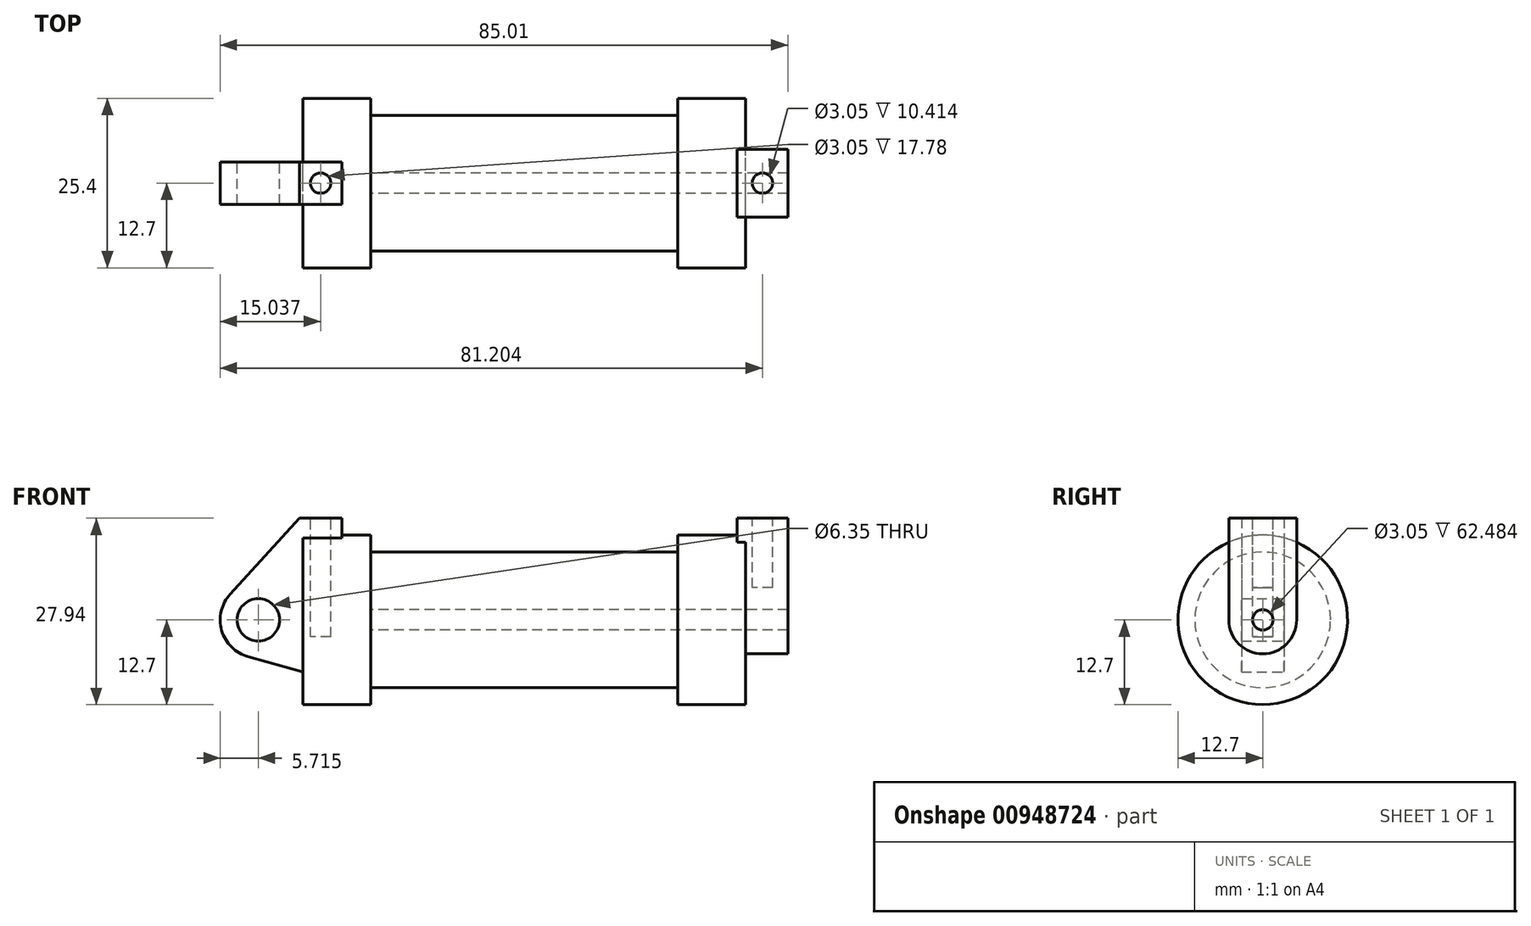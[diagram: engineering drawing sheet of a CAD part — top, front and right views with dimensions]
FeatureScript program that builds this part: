
annotation { "Feature Type Name" : "Feature", "Feature Type Description" : "" }
export const myFeature = defineFeature(function(context is Context, id is Id, definition is map)
    precondition{}
    {
        {
            var Q0;
            Q0=qCreatedBy(makeId("Front.planeOp"),FACE);
            var sketch = newSketch(context, id + "F0", { "sketchPlane" : qUnion([Q0])});
            skLineSegment(sketch, "E0", {"start": v(0, 0) * mm, "end": v(0, 12.7) * mm});
            skLineSegment(sketch, "E1", {"start": v(0, 12.7) * mm, "end": v(10.16, 12.7) * mm});
            skLineSegment(sketch, "E2", {"start": v(10.16, 12.7) * mm, "end": v(10.16, 10.16) * mm});
            skLineSegment(sketch, "E3", {"start": v(10.16, 10.16) * mm, "end": v(56.13, 10.16) * mm});
            skLineSegment(sketch, "E4", {"start": v(56.13, 10.16) * mm, "end": v(56.13, 12.7) * mm});
            skLineSegment(sketch, "E5", {"start": v(56.13, 12.7) * mm, "end": v(66.3, 12.7) * mm});
            skLineSegment(sketch, "E6", {"start": v(66.3, 12.7) * mm, "end": v(66.3, 0) * mm});
            skLineSegment(sketch, "E7", {"start": v(66.3, 0) * mm, "end": v(0, 0) * mm});
            skLineSegment(sketch, "E8", {"start": v(5.84, 15.24) * mm, "end": v(-0.5, 15.24) * mm});
            skLineSegment(sketch, "E9", {"start": v(-0.5, 15.24) * mm, "end": v(-10.88, 3.85) * mm});
            skLineSegment(sketch, "E10", {"start": v(0, 0) * mm, "end": v(-6.65, 0) * mm});
            skCircle(sketch, "E11", {"center": v(-6.65, 0) * mm, "radius": 5.72 * mm});
            skCircle(sketch, "E12", {"center": v(-6.65, 0) * mm, "radius": 3.18 * mm});
            skLineSegment(sketch, "E13", {"start": v(5.84, 15.24) * mm, "end": v(5.84, -9.4) * mm});
            skLineSegment(sketch, "E14", {"start": v(5.84, -9.4) * mm, "end": v(-8.18, -5.5) * mm});
            skSolve(sketch);
        }
        {
            var Q0;
            {var subQ0=sQuery(id+"F0.wireOp",EDGE,"E2");Q0=makeQuery(id+"F0.imprint","IMPRINT",FACE,{"disambiguationData":[TD([[makeQuery(id+"F0.imprint","IMPRINT",EDGE,{"derivedFrom":subQ0}),-1.0]])]});}
            var Q1;
            {var subQ0=sQuery(id+"F0.wireOp",EDGE,"E0");Q1=makeQuery(id+"F0.imprint","IMPRINT",FACE,{"disambiguationData":[TD([[makeQuery(id+"F0.imprint","IMPRINT",EDGE,{"derivedFrom":subQ0}),-1.0]])]});}
            var Q2;
            Q2=sQuery(id+"F0.wireOp",EDGE,"E7");
            revolve(context, id + "F1", {"surfaceOperationType" : NewSurfaceOperationType.NEW, "entities" : qUnion([Q0, Q1]), "axis" : qUnion([Q2]), "revolveType" : RevolveType.FULL});
        }
        {
            var Q0;
            {var subQ0=sQuery(id+"F0.wireOp",EDGE,"E0");Q0=makeQuery(id+"F0.imprint","IMPRINT",FACE,{"disambiguationData":[TD([[makeQuery(id+"F0.imprint","IMPRINT",EDGE,{"derivedFrom":subQ0}),-1.0]])]});}
            var Q1;
            {var subQ1=sQuery(id+"F0.wireOp",EDGE,"E0");Q1=makeQuery(id+"F0.imprint","IMPRINT",FACE,{"disambiguationData":[TD([[makeQuery(id+"F0.imprint","IMPRINT",EDGE,{"derivedFrom":subQ1}),1.0]])]});}
            var Q2;
            {var subQ0=sQuery(id+"F0.wireOp",EDGE,"E14");Q2=makeQuery(id+"F0.imprint","IMPRINT",FACE,{"disambiguationData":[TD([[makeQuery(id+"F0.imprint","IMPRINT",EDGE,{"derivedFrom":subQ0}),-1.0]])]});}
            var Q3;
            {var subQ5=sQuery(id+"F0.wireOp",EDGE,"E12");Q3=makeQuery(id+"F0.imprint","IMPRINT",FACE,{"disambiguationData":[TD([[makeQuery(id+"F0.imprint","IMPRINT",EDGE,{"derivedFrom":subQ5}),-1.0]])]});}
            extrude(context, id + "F2", {"entities" : qUnion([Q0, Q1, Q2, Q3]), "operationType" : NewBodyOperationType.ADD, "endBound" : BoundingType.SYMMETRIC, "depth" : 6.35 * mm, "offsetDistance" : 25.4 * mm});
        }
        {
            var Q0;
            Q0=makeQuery(id+"F1.opRevolve","SWEPT_FACE",FACE,{"disambiguationData":[OSD([sQuery(id+"F0.wireOp",EDGE,"E6")])]});
            var sketch = newSketch(context, id + "F3", { "sketchPlane" : qUnion([Q0])});
            skCircle(sketch, "E15", {"center": v(0, 0) * mm, "radius": 1.52 * mm});
            skCircle(sketch, "E16", {"center": v(0, 0) * mm, "radius": 5.08 * mm});
            skLineSegment(sketch, "E17.0", {"start": v(-3.18, 15.24) * mm, "end": v(3.17, 15.24) * mm});
            skPoint(sketch, "E18.endSnap0", {"position": v(0, 15.24) * mm});
            skLineSegment(sketch, "E19", {"start": v(-5.08, 0) * mm, "end": v(-5.08, 15.24) * mm});
            skLineSegment(sketch, "E20", {"start": v(5.08, 0) * mm, "end": v(5.08, 15.24) * mm});
            skLineSegment(sketch, "E21", {"start": v(-5.08, 15.24) * mm, "end": v(5.08, 15.24) * mm});
            skSolve(sketch);
        }
        {
            var Q0;
            Q0=makeQuery(id+"F3.imprint","IMPRINT",FACE,{"disambiguationData":[TD([[makeQuery(id+"F3.imprint","IMPRINT",EDGE,{"derivedFrom":sQuery(id+"F3.wireOp",EDGE,"E15")}),1.0]])]});
            var Q1;
            Q1=makeQuery(id+"F3.imprint","IMPRINT",FACE,{"disambiguationData":[TD([[makeQuery(id+"F3.imprint","IMPRINT",EDGE,{"derivedFrom":sQuery(id+"F3.wireOp",EDGE,"E15")}),-1.0]])]});
            var Q2;
            {var subQ0=sQuery(id+"F3.wireOp",EDGE,"E19");var subQ1=sQuery(id+"F3.wireOp",EDGE,"E16");var subQ2=makeQuery(id+"F3.imprint","INTERSECT",VERTEX,{"derivedFrom":[subQ1,subQ0]});Q2=makeQuery(id+"F3.imprint","IMPRINT",FACE,{"disambiguationData":[TD([[makeQuery(id+"F3.imprint","IMPRINT",EDGE,{"disambiguationData":[TD([[subQ2,1.0]])],"derivedFrom":subQ1}),-1.0]])]});}
            var Q3;
            {var subQ0=sQuery(id+"F3.wireOp",EDGE,"E21");var subQ1=sQuery(id+"F3.wireOp",EDGE,"E19");var subQ2=makeQuery(id+"F3.imprint","INTERSECT",VERTEX,{"derivedFrom":[subQ1,subQ0]});Q3=makeQuery(id+"F3.imprint","IMPRINT",FACE,{"disambiguationData":[TD([[makeQuery(id+"F3.imprint","IMPRINT",EDGE,{"disambiguationData":[TD([[subQ2,-1.0]])],"derivedFrom":subQ0}),-1.0]])]});}
            extrude(context, id + "F4", {"entities" : qUnion([Q0, Q1, Q2, Q3]), "operationType" : NewBodyOperationType.ADD, "depth" : 6.35 * mm, "offsetDistance" : 25.4 * mm});
        }
        {
            var Q0;
            Q0 = qSketchRegion(id + "F3", true);
            extrude(context, id + "F5", {"entities" : qUnion([Q0]), "operationType" : NewBodyOperationType.ADD, "oppositeDirection" : true, "depth" : 1.27 * mm, "offsetDistance" : 25.4 * mm});
        }
        {
            var Q0;
            Q0=makeQuery(id+"F3.imprint","IMPRINT",FACE,{"disambiguationData":[TD([[makeQuery(id+"F3.imprint","IMPRINT",EDGE,{"derivedFrom":sQuery(id+"F3.wireOp",EDGE,"E15")}),1.0]])]});
            extrude(context, id + "F6", {"entities" : qUnion([Q0]), "operationType" : NewBodyOperationType.REMOVE, "depth" : 6.35 * mm, "offsetDistance" : 25.4 * mm});
        }
        {
            var Q0;
            Q0=makeQuery(id+"F3.imprint","IMPRINT",FACE,{"disambiguationData":[TD([[makeQuery(id+"F3.imprint","IMPRINT",EDGE,{"derivedFrom":sQuery(id+"F3.wireOp",EDGE,"E15")}),1.0]])]});
            var Q1;
            Q1=makeQuery(id+"F1.opRevolve","SWEPT_FACE",FACE,{"disambiguationData":[OSD([sQuery(id+"F0.wireOp",EDGE,"E2")])]});
            extrude(context, id + "F7", {"entities" : qUnion([Q0]), "operationType" : NewBodyOperationType.REMOVE, "endBound" : BoundingType.UP_TO_SURFACE, "oppositeDirection" : true, "depth" : 25.4 * mm, "endBoundEntityFace" : qUnion([Q1]), "offsetDistance" : 25.4 * mm});
        }
        {
            var Q0;
            {var subQ0=sQuery(id+"F3.wireOp",EDGE,"E21");Q0=makeQuery(id+"F5.boolean.opBoolean","MERGE",FACE,{"derivedFrom":[makeQuery(id+"F4.opExtrude","SWEPT_FACE",FACE,{"disambiguationData":[OSD([subQ0])]}),makeQuery(id+"F5.opExtrude","SWEPT_FACE",FACE,{"disambiguationData":[OSD([subQ0])]})]});}
            var sketch = newSketch(context, id + "F8", { "sketchPlane" : qUnion([Q0])});
            skCircle(sketch, "E22", {"center": v(68.83, 0) * mm, "radius": 1.52 * mm});
            skSolve(sketch);
        }
        {
            var Q0;
            Q0=makeQuery(id+"F8.imprint","IMPRINT",FACE,{"disambiguationData":[TD([[makeQuery(id+"F8.imprint","IMPRINT",EDGE,{"derivedFrom":sQuery(id+"F8.wireOp",EDGE,"E22")}),1.0]])]});
            extrude(context, id + "F9", {"entities" : qUnion([Q0]), "operationType" : NewBodyOperationType.REMOVE, "oppositeDirection" : true, "depth" : 10.4 * mm, "offsetDistance" : 25.4 * mm});
        }
        {
            var Q0;
            Q0=makeQuery(id+"F2.opExtrude","SWEPT_FACE",FACE,{"disambiguationData":[OSD([sQuery(id+"F0.wireOp",EDGE,"E8")])]});
            var sketch = newSketch(context, id + "F10", { "sketchPlane" : qUnion([Q0])});
            skCircle(sketch, "E23", {"center": v(2.67, 0) * mm, "radius": 1.52 * mm});
            skSolve(sketch);
        }
        {
            var Q0;
            Q0=makeQuery(id+"F10.imprint","IMPRINT",FACE,{"disambiguationData":[TD([[makeQuery(id+"F10.imprint","IMPRINT",EDGE,{"derivedFrom":sQuery(id+"F10.wireOp",EDGE,"E23")}),1.0]])]});
            extrude(context, id + "F11", {"entities" : qUnion([Q0]), "operationType" : NewBodyOperationType.REMOVE, "oppositeDirection" : true, "depth" : 17.78 * mm, "offsetDistance" : 25.4 * mm});
        }
    });
